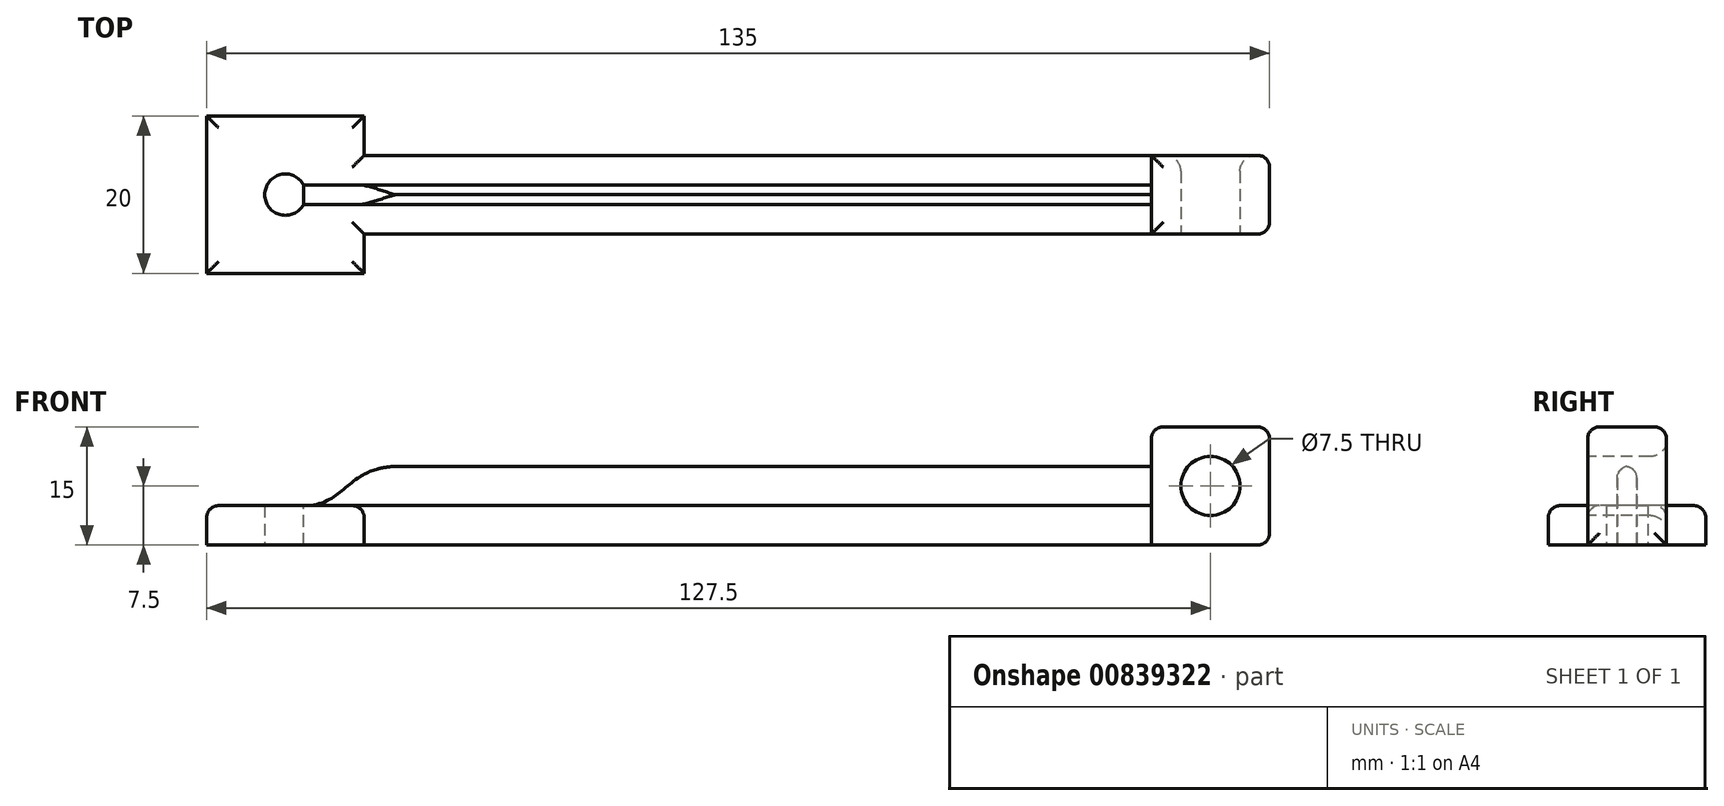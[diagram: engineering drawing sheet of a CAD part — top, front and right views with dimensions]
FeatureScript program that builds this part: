
annotation { "Feature Type Name" : "Feature", "Feature Type Description" : "" }
export const myFeature = defineFeature(function(context is Context, id is Id, definition is map)
    precondition{}
    {
        {
            var Q0;
            Q0=qCreatedBy(makeId("Top.planeOp"),FACE);
            var sketch = newSketch(context, id + "F0", { "sketchPlane" : qUnion([Q0])});
            skLineSegment(sketch, "E0.bottom", {"start": v(-10, 10) * mm, "end": v(10, 10) * mm});
            skLineSegment(sketch, "E0.top", {"start": v(-10, -10) * mm, "end": v(10, -10) * mm});
            skLineSegment(sketch, "E0.left", {"start": v(-10, 10) * mm, "end": v(-10, -10) * mm});
            skLineSegment(sketch, "E0.right", {"start": v(10, 10) * mm, "end": v(10, -10) * mm});
            skPoint(sketch, "E0.middle", {"position": v(0, 0) * mm});
            skLineSegment(sketch, "E1", {"start": v(-10, 0) * mm, "end": v(10, 0) * mm, "construction": true});
            skLineSegment(sketch, "E2", {"start": v(10, 0) * mm, "end": v(0, 10) * mm, "construction": true});
            skLineSegment(sketch, "E3", {"start": v(5, 5) * mm, "end": v(10, 5) * mm, "construction": true});
            skLineSegment(sketch, "E4", {"start": v(10, 0) * mm, "end": v(0, -10) * mm, "construction": true});
            skLineSegment(sketch, "E5", {"start": v(5, -5) * mm, "end": v(10, -5) * mm, "construction": true});
            skLineSegment(sketch, "E6.bottom", {"start": v(10, 5) * mm, "end": v(110, 5) * mm});
            skLineSegment(sketch, "E6.top", {"start": v(10, -5) * mm, "end": v(110, -5) * mm});
            skLineSegment(sketch, "E6.left", {"start": v(10, 5) * mm, "end": v(10, -5) * mm});
            skLineSegment(sketch, "E6.right", {"start": v(110, 5) * mm, "end": v(110, -5) * mm});
            skLineSegment(sketch, "E7.bottom", {"start": v(110, 5) * mm, "end": v(125, 5) * mm});
            skLineSegment(sketch, "E7.top", {"start": v(110, -5) * mm, "end": v(125, -5) * mm});
            skLineSegment(sketch, "E7.right", {"start": v(125, 5) * mm, "end": v(125, -5) * mm});
            skLineSegment(sketch, "E8.left", {"start": v(2.1, 5.96) * mm, "end": v(0.24, 1.78) * mm, "construction": true});
            skLineSegment(sketch, "E9.left", {"start": v(0, 78.73) * mm, "end": v(-26.7, 68.72) * mm});
            skCircle(sketch, "E10", {"center": v(0, 0) * mm, "radius": 2.62 * mm});
            skLineSegment(sketch, "E11.bottom", {"start": v(0, 1.25) * mm, "end": v(110, 1.25) * mm});
            skLineSegment(sketch, "E11.top", {"start": v(0, -1.25) * mm, "end": v(110, -1.25) * mm});
            skLineSegment(sketch, "E11.left", {"start": v(0, 1.25) * mm, "end": v(0, -1.25) * mm});
            skLineSegment(sketch, "E11.right", {"start": v(110, 1.25) * mm, "end": v(110, -1.25) * mm});
            skSolve(sketch);
        }
        {
            var Q0;
            {var subQ1=sQuery(id+"F0.wireOp",EDGE,"E0.bottom");Q0=makeQuery(id+"F0.imprint","IMPRINT",FACE,{"disambiguationData":[TD([[makeQuery(id+"F0.imprint","IMPRINT",EDGE,{"derivedFrom":subQ1}),-1.0]])]});}
            var Q1;
            {var subQ5=sQuery(id+"F0.wireOp",EDGE,"E6.bottom");Q1=makeQuery(id+"F0.imprint","IMPRINT",FACE,{"disambiguationData":[TD([[makeQuery(id+"F0.imprint","IMPRINT",EDGE,{"derivedFrom":subQ5}),-1.0]])]});}
            var Q2;
            {var subQ4=sQuery(id+"F0.wireOp",EDGE,"E6.top");Q2=makeQuery(id+"F0.imprint","IMPRINT",FACE,{"disambiguationData":[TD([[makeQuery(id+"F0.imprint","IMPRINT",EDGE,{"derivedFrom":subQ4}),1.0]])]});}
            extrude(context, id + "F1", {"entities" : qUnion([Q0, Q1, Q2]), "offsetDistance" : 25 * mm, "depth" : 5 * mm});
        }
        {
            var Q0;
            Q0=makeQuery(id+"F0.imprint","IMPRINT",FACE,{"disambiguationData":[TD([[makeQuery(id+"F0.imprint","IMPRINT",EDGE,{"derivedFrom":sQuery(id+"F0.wireOp",EDGE,"E11.bottom")}),-1.0]])]});
            extrude(context, id + "F2", {"entities" : qUnion([Q0]), "depth" : 10 * mm});
        }
        {
            var Q0;
            {var subQ3=sQuery(id+"F0.wireOp",EDGE,"E7.bottom");Q0=makeQuery(id+"F0.imprint","IMPRINT",FACE,{"disambiguationData":[TD([[makeQuery(id+"F0.imprint","IMPRINT",EDGE,{"derivedFrom":subQ3}),-1.0]])]});}
            extrude(context, id + "F3", {"entities" : qUnion([Q0]), "depth" : 15 * mm});
        }
        {
            var Q0;
            Q0=makeQuery(id+"F3.opExtrude","SWEPT_FACE",FACE,{"disambiguationData":[OSD([sQuery(id+"F0.wireOp",EDGE,"E7.top")])]});
            var sketch = newSketch(context, id + "F4", { "sketchPlane" : qUnion([Q0])});
            skCircle(sketch, "E12", {"center": v(117.5, 7.5) * mm, "radius": 10.6 * mm});
            skPoint(sketch, "E12.centerSnap0", {"position": v(117.5, 0) * mm});
            skPoint(sketch, "E12.centerSnap1", {"position": v(110, 7.5) * mm});
            skLineSegment(sketch, "E13.0.0", {"start": v(110, 0) * mm, "end": v(125, 0) * mm});
            skLineSegment(sketch, "E13.0.1", {"start": v(125, 0) * mm, "end": v(125, 15) * mm});
            skLineSegment(sketch, "E13.0.2", {"start": v(110, 15) * mm, "end": v(110, 15) * mm});
            skLineSegment(sketch, "E13.0.3", {"start": v(110, 15) * mm, "end": v(110, 0) * mm});
            skCircle(sketch, "E14", {"center": v(117.5, 7.5) * mm, "radius": 3.75 * mm});
            skSolve(sketch);
        }
        {
            var Q0;
            Q0=makeQuery(id+"F4.imprint","IMPRINT",FACE,{"disambiguationData":[TD([[makeQuery(id+"F4.imprint","IMPRINT",EDGE,{"derivedFrom":sQuery(id+"F4.wireOp",EDGE,"E14")}),1.0]])]});
            extrude(context, id + "F5", {"entities" : qUnion([Q0]), "operationType" : NewBodyOperationType.REMOVE, "oppositeDirection" : true, "depth" : 30.02 * mm});
        }
        {
            var Q0;
            Q0=makeQuery(id+"F3.opExtrude","CAP_EDGE",EDGE,{"disambiguationData":[OSD([sQuery(id+"F0.wireOp",EDGE,"E6.right"),sQuery(id+"F0.wireOp",EDGE,"E9.right")])],"isStart":false});
            var Q1;
            Q1=makeQuery(id+"F3.opExtrude","CAP_EDGE",EDGE,{"disambiguationData":[OSD([sQuery(id+"F0.wireOp",EDGE,"E7.right")])],"isStart":false});
            var Q2;
            Q2=makeQuery(id+"F3.opExtrude","CAP_EDGE",EDGE,{"disambiguationData":[OSD([sQuery(id+"F0.wireOp",EDGE,"E7.right")])],"isStart":true});
            var Q3;
            Q3=makeQuery(id+"F3.opExtrude","CAP_EDGE",EDGE,{"disambiguationData":[OSD([sQuery(id+"F0.wireOp",EDGE,"E7.top")])],"isStart":false});
            var Q4;
            Q4=makeQuery(id+"F3.opExtrude","SWEPT_EDGE",EDGE,{"disambiguationData":[OSD([sQuery(id+"F0.wireOp",EDGE,"E7.top"),sQuery(id+"F0.wireOp",EDGE,"E7.right")])]});
            var Q5;
            Q5=makeQuery(id+"F3.opExtrude","CAP_EDGE",EDGE,{"disambiguationData":[OSD([sQuery(id+"F0.wireOp",EDGE,"E7.bottom")])],"isStart":false});
            var Q6;
            Q6=makeQuery(id+"F3.opExtrude","SWEPT_EDGE",EDGE,{"disambiguationData":[OSD([sQuery(id+"F0.wireOp",EDGE,"E7.bottom"),sQuery(id+"F0.wireOp",EDGE,"E7.right")])]});
            fillet(context, id + "F6", {"entities" : qUnion([Q0, Q1, Q2, Q3, Q4, Q5, Q6]), "radius" : 1.5 * mm, "tangentPropagation" : true, "allowEdgeOverflow" : false});
        }
        {
            var Q0;
            Q0=makeQuery(id+"F2.opExtrude","CAP_EDGE",EDGE,{"disambiguationData":[OSD([sQuery(id+"F0.wireOp",EDGE,"E9.top")])],"isStart":false});
            var Q1;
            Q1=makeQuery(id+"F2.opExtrude","CAP_EDGE",EDGE,{"disambiguationData":[OSD([sQuery(id+"F0.wireOp",EDGE,"E9.bottom")])],"isStart":false});
            var Q2;
            Q2=makeQuery(id+"F1.opExtrude","CAP_EDGE",EDGE,{"disambiguationData":[OSD([sQuery(id+"F0.wireOp",EDGE,"E6.top")])],"isStart":false});
            var Q3;
            Q3=makeQuery(id+"F1.opExtrude","CAP_EDGE",EDGE,{"disambiguationData":[OSD([sQuery(id+"F0.wireOp",EDGE,"E6.bottom")])],"isStart":false});
            var Q4;
            Q4=makeQuery(id+"F1.opExtrude","CAP_EDGE",EDGE,{"disambiguationData":[OSD([sQuery(id+"F0.wireOp",EDGE,"E0.bottom")])],"isStart":false});
            var Q5;
            {var subQ0=sQuery(id+"F0.wireOp",EDGE,"E0.right");Q5=makeQuery(id+"F1.opExtrude","CAP_EDGE",EDGE,{"disambiguationData":[OSD([subQ0]),TDD([makeQuery(id+"F0.imprint","IMPRINT",EDGE,{"disambiguationData":[TD([[makeQuery(id+"F0.imprint","INTERSECT",VERTEX,{"derivedFrom":[sQuery(id+"F0.wireOp",EDGE,"E0.bottom"),subQ0]}),-1.0]])],"derivedFrom":subQ0})])],"isStart":false});}
            var Q6;
            {var subQ0=sQuery(id+"F0.wireOp",EDGE,"E0.right");Q6=makeQuery(id+"F1.opExtrude","CAP_EDGE",EDGE,{"disambiguationData":[OSD([subQ0]),TDD([makeQuery(id+"F0.imprint","IMPRINT",EDGE,{"disambiguationData":[TD([[makeQuery(id+"F0.imprint","INTERSECT",VERTEX,{"derivedFrom":[sQuery(id+"F0.wireOp",EDGE,"E0.top"),subQ0]}),1.0]])],"derivedFrom":subQ0})])],"isStart":false});}
            var Q7;
            Q7=makeQuery(id+"F1.opExtrude","CAP_EDGE",EDGE,{"disambiguationData":[OSD([sQuery(id+"F0.wireOp",EDGE,"E0.top")])],"isStart":false});
            var Q8;
            Q8=makeQuery(id+"F1.opExtrude","CAP_EDGE",EDGE,{"disambiguationData":[OSD([sQuery(id+"F0.wireOp",EDGE,"E0.left")])],"isStart":false});
            var Q9;
            Q9=makeQuery(id+"F2.opExtrude","CAP_EDGE",EDGE,{"disambiguationData":[OSD([sQuery(id+"F0.wireOp",EDGE,"E11.top")])],"isStart":false});
            var Q10;
            Q10=makeQuery(id+"F2.opExtrude","CAP_EDGE",EDGE,{"disambiguationData":[OSD([sQuery(id+"F0.wireOp",EDGE,"E11.bottom")])],"isStart":false});
            fillet(context, id + "F7", {"entities" : qUnion([Q0, Q1, Q2, Q3, Q4, Q5, Q6, Q7, Q8, Q9, Q10]), "radius" : 1.5 * mm, "tangentPropagation" : true, "allowEdgeOverflow" : false});
        }
        {
            var Q0;
            Q0=makeQuery(id+"F2.opExtrude","SWEPT_FACE",FACE,{"disambiguationData":[OSD([sQuery(id+"F0.wireOp",EDGE,"E11.top")])]});
            var sketch = newSketch(context, id + "F8", { "sketchPlane" : qUnion([Q0])});
            skLineSegment(sketch, "E15.0", {"start": v(2.3, 5) * mm, "end": v(110, 5) * mm});
            skLineSegment(sketch, "E16", {"start": v(2.3, 5) * mm, "end": v(0, 5) * mm});
            skLineSegment(sketch, "E17.0.0", {"start": v(0, 8.5) * mm, "end": v(0, 9.98) * mm});
            skLineSegment(sketch, "E17.0.1", {"start": v(110, 8.5) * mm, "end": v(0, 8.5) * mm});
            skLineSegment(sketch, "E17.0.2", {"start": v(110, 8.5) * mm, "end": v(110, 9.98) * mm});
            skLineSegment(sketch, "E17.0.3", {"start": v(110, 9.98) * mm, "end": v(0, 9.98) * mm});
            skLineSegment(sketch, "E18.0.0", {"start": v(110, 0) * mm, "end": v(110, 8.5) * mm});
            skLineSegment(sketch, "E18.0.2", {"start": v(0, 8.5) * mm, "end": v(0, 0) * mm});
            skLineSegment(sketch, "E18.0.3", {"start": v(0, 0) * mm, "end": v(110, 0) * mm});
            skFitSpline(sketch, "E19", {"points": [v(2.3, 5) * mm, v(14.36, 9.98) * mm], "startDerivative": vector(16.34, 0) * mm, "endDerivative": vector(19.8, 0) * mm});
            skSolve(sketch);
        }
        {
            var Q0;
            {var subQ0=sQuery(id+"F8.wireOp",EDGE,"E16");Q0=makeQuery(id+"F8.imprint","IMPRINT",FACE,{"disambiguationData":[TD([[makeQuery(id+"F8.imprint","IMPRINT",EDGE,{"derivedFrom":subQ0}),-1.0]])]});}
            var Q1;
            {var subQ0=sQuery(id+"F8.wireOp",EDGE,"E17.0.0");Q1=makeQuery(id+"F8.imprint","IMPRINT",FACE,{"disambiguationData":[TD([[makeQuery(id+"F8.imprint","IMPRINT",EDGE,{"derivedFrom":subQ0}),-1.0]])]});}
            extrude(context, id + "F9", {"entities" : qUnion([Q0, Q1]), "operationType" : NewBodyOperationType.REMOVE, "oppositeDirection" : true, "depth" : 25 * mm});
        }
        {
            var Q0;
            {var subQ5=sQuery(id+"F0.wireOp",EDGE,"E11.left");Q0=makeQuery(id+"F0.imprint","IMPRINT",FACE,{"disambiguationData":[TD([[makeQuery(id+"F0.imprint","IMPRINT",EDGE,{"derivedFrom":subQ5}),-1.0]])]});}
            var Q1;
            Q1=makeQuery(id+"F9.boolean.opBoolean","COPY",FACE,{"derivedFrom":makeQuery(id+"F9.opExtrude","SWEPT_FACE",FACE,{"disambiguationData":[OSD([sQuery(id+"F8.wireOp",EDGE,"Xsfl9bUJ-CShi-Uoxw-aEfo-lC1LjiXzIiVe")])]})});
            var Q2;
            Q2=makeQuery(id+"F9.boolean.opBoolean","COPY",FACE,{"derivedFrom":makeQuery(id+"F9.opExtrude","SWEPT_FACE",FACE,{"disambiguationData":[OSD([sQuery(id+"F8.wireOp",EDGE,"E16")])]})});
            extrude(context, id + "F10", {"entities" : qUnion([Q0, Q1, Q2]), "operationType" : NewBodyOperationType.REMOVE, "oppositeDirection" : true, "depth" : 25 * mm});
        }
        {
            var Q0;
            Q0=makeQuery(id+"F5.boolean.opBoolean","COPY",EDGE,{"derivedFrom":makeQuery(id+"F5.opExtrude","CAP_EDGE",EDGE,{"disambiguationData":[OSD([sQuery(id+"F4.wireOp",EDGE,"E14")])],"isStart":true})});
            var Q1;
            Q1=makeQuery(id+"F5.boolean.opBoolean","INTERSECT",EDGE,{"derivedFrom":[makeQuery(id+"F3.opExtrude","SWEPT_FACE",FACE,{"disambiguationData":[OSD([sQuery(id+"F0.wireOp",EDGE,"E7.bottom")])]}),makeQuery(id+"F5.opExtrude","SWEPT_FACE",FACE,{"disambiguationData":[OSD([sQuery(id+"F4.wireOp",EDGE,"E14")])]})]});
            fillet(context, id + "F11", {"entities" : qUnion([Q0, Q1]), "radius" : 2 * mm, "tangentPropagation" : true, "allowEdgeOverflow" : false});
        }
    });
